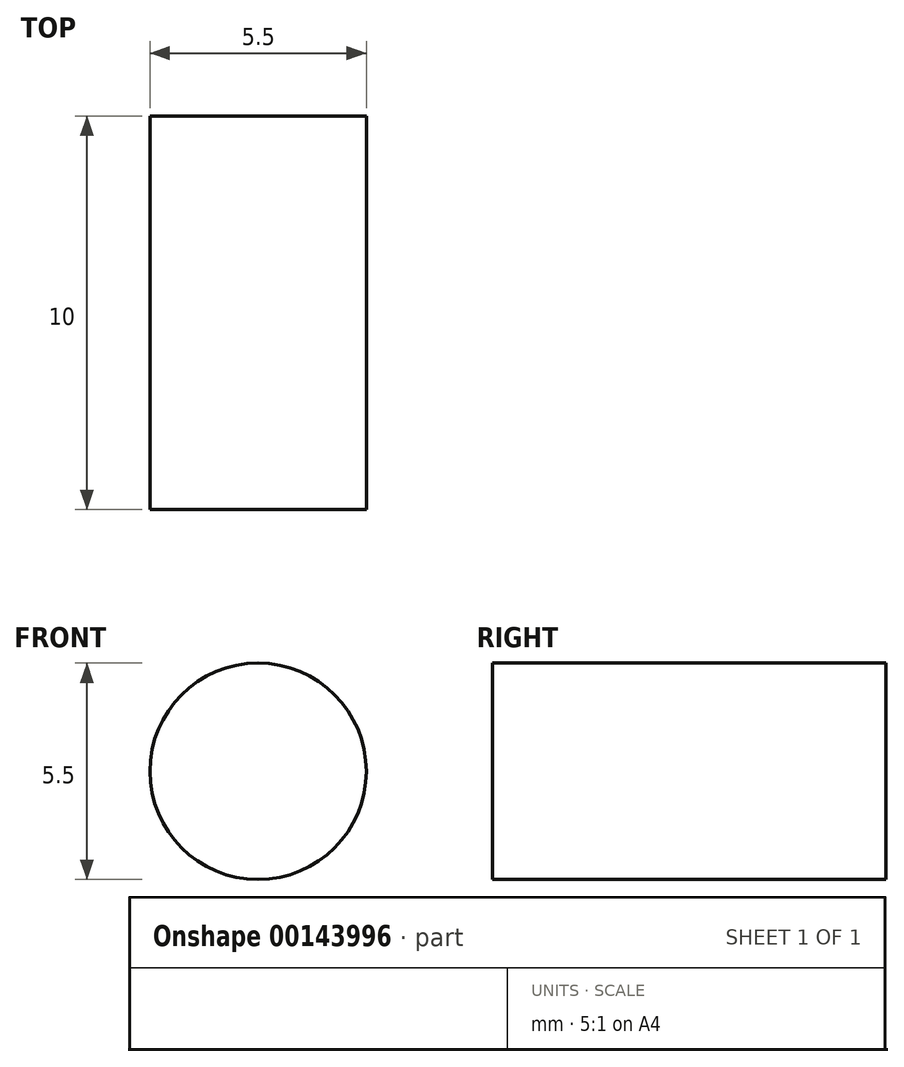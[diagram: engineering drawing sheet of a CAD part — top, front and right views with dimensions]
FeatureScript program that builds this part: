
annotation { "Feature Type Name" : "Feature", "Feature Type Description" : "" }
export const myFeature = defineFeature(function(context is Context, id is Id, definition is map)
    precondition{}
    {
        {
            var Q0;
            Q0=qCreatedBy(makeId("Front.planeOp"),FACE);
            var sketch = newSketch(context, id + "F0", { "sketchPlane" : qUnion([Q0])});
            skCircle(sketch, "E0", {"center": v(0, 0) * mm, "radius": 2.75 * mm});
            skSolve(sketch);
        }
        {
            var Q0;
            Q0=qSketchRegion(id+"F0",true);
            extrude(context, id + "F1", {"entities" : qUnion([Q0]), "depth" : 10 * mm});
        }
    });
